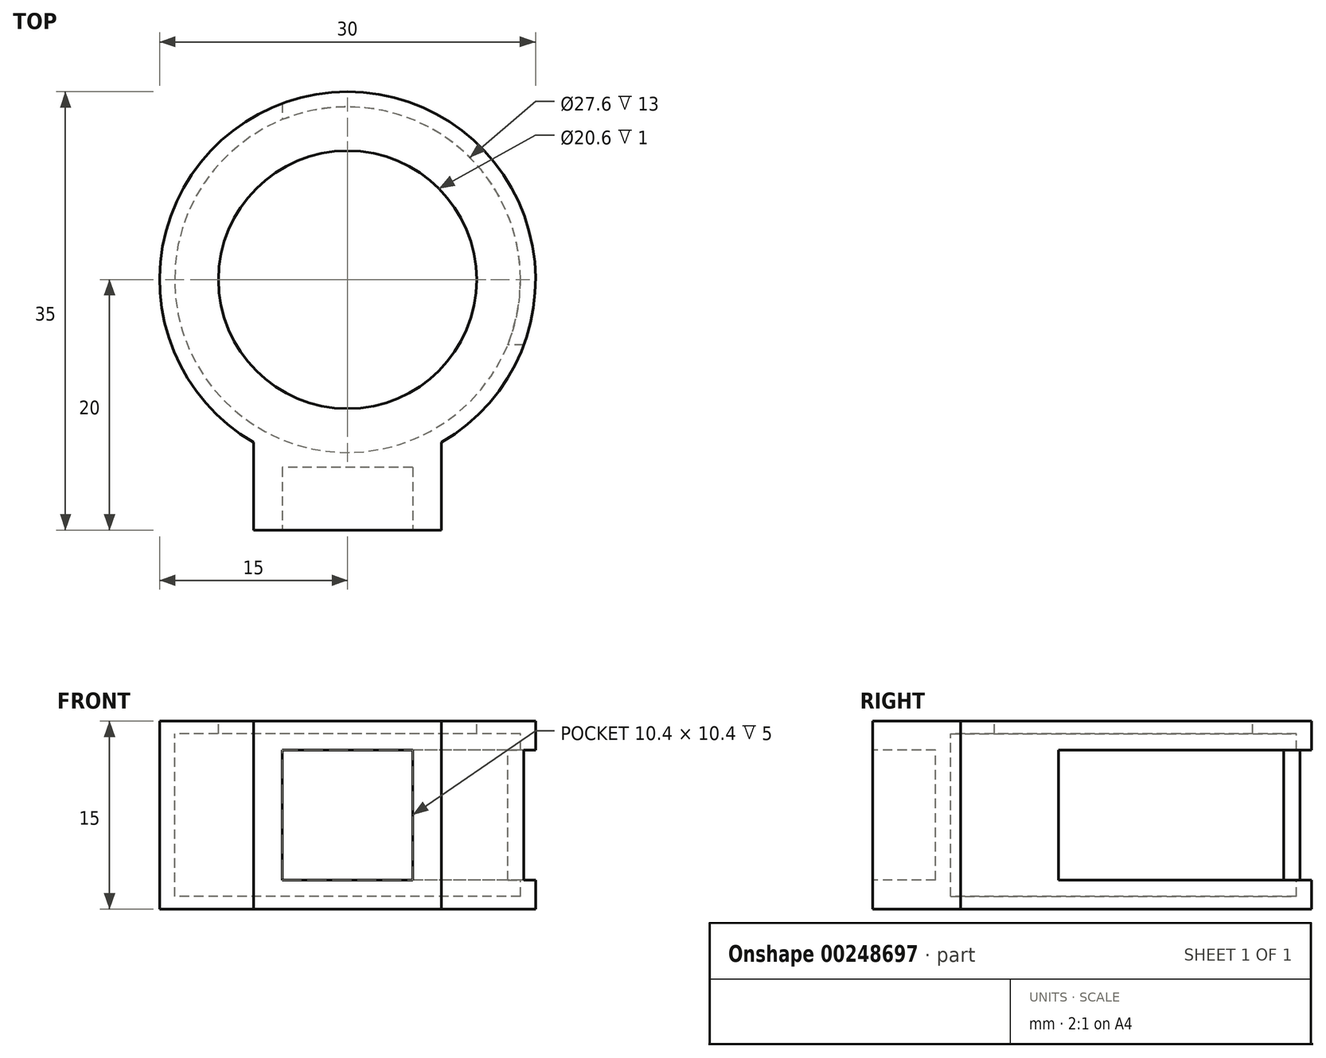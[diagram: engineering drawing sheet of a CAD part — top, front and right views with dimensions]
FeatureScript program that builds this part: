
annotation { "Feature Type Name" : "Feature", "Feature Type Description" : "" }
export const myFeature = defineFeature(function(context is Context, id is Id, definition is map)
    precondition{}
    {
        {
            var Q0;
            Q0=qCreatedBy(makeId("Top.planeOp"),FACE);
            var sketch = newSketch(context, id + "F0", { "sketchPlane" : qUnion([Q0])});
            skCircle(sketch, "E0", {"center": v(0, 0) * mm, "radius": 15 * mm});
            skSolve(sketch);
        }
        {
            var Q0;
            Q0 = qSketchRegion(id + "F0", true);
            extrude(context, id + "F1", {"entities" : qUnion([Q0]), "depth" : 15 * mm});
        }
        {
            var Q0;
            Q0=qCreatedBy(makeId("Front.planeOp"),FACE);
            var sketch = newSketch(context, id + "F2", { "sketchPlane" : qUnion([Q0])});
            skLineSegment(sketch, "E1.bottom", {"start": v(7.5, 0) * mm, "end": v(-7.5, 0) * mm});
            skLineSegment(sketch, "E1.top", {"start": v(7.5, 15) * mm, "end": v(-7.5, 15) * mm});
            skLineSegment(sketch, "E1.left", {"start": v(7.5, 0) * mm, "end": v(7.5, 15) * mm});
            skLineSegment(sketch, "E1.right", {"start": v(-7.5, 0) * mm, "end": v(-7.5, 15) * mm});
            skPoint(sketch, "E1.middle", {"position": v(0, 7.5) * mm});
            skSolve(sketch);
        }
        {
            var Q0;
            Q0 = qSketchRegion(id + "F2", true);
            extrude(context, id + "F3", {"entities" : qUnion([Q0]), "operationType" : NewBodyOperationType.ADD, "depth" : 20 * mm});
        }
        {
            var Q0;
            Q0=makeQuery(id+"F3.opExtrude","CAP_FACE",FACE,{"disambiguationData":[OSD([sQuery(id+"F2.wireOp",EDGE,"E1.bottom"),sQuery(id+"F2.wireOp",EDGE,"E1.top"),sQuery(id+"F2.wireOp",EDGE,"E1.left"),sQuery(id+"F2.wireOp",EDGE,"E1.right")])],"isStart":false});
            var sketch = newSketch(context, id + "F4", { "sketchPlane" : qUnion([Q0])});
            skLineSegment(sketch, "E2.bottom", {"start": v(5.2, 2.3) * mm, "end": v(-5.2, 2.3) * mm});
            skLineSegment(sketch, "E2.top", {"start": v(5.2, 12.7) * mm, "end": v(-5.2, 12.7) * mm});
            skLineSegment(sketch, "E2.left", {"start": v(5.2, 2.3) * mm, "end": v(5.2, 12.7) * mm});
            skLineSegment(sketch, "E2.right", {"start": v(-5.2, 2.3) * mm, "end": v(-5.2, 12.7) * mm});
            skPoint(sketch, "E2.middle", {"position": v(0, 7.5) * mm});
            skPoint(sketch, "E2.middle.positionSnap0", {"position": v(0, 15) * mm});
            skPoint(sketch, "E2.middle.positionSnap1", {"position": v(-7.5, 7.5) * mm});
            skPoint(sketch, "E2.centerSnap0", {"position": v(0, 15) * mm});
            skPoint(sketch, "E2.centerSnap1", {"position": v(-7.5, 7.5) * mm});
            skSolve(sketch);
        }
        {
            var Q0;
            Q0 = qSketchRegion(id + "F4", true);
            extrude(context, id + "F5", {"entities" : qUnion([Q0]), "operationType" : NewBodyOperationType.REMOVE, "oppositeDirection" : true, "depth" : 5 * mm});
        }
        {
            var Q0;
            Q0=makeQuery(id+"F3.boolean.opBoolean","MERGE",FACE,{"derivedFrom":[makeQuery(id+"F1.opExtrude","CAP_FACE",FACE,{"disambiguationData":[OSD([sQuery(id+"F0.wireOp",EDGE,"E0")])],"isStart":false}),makeQuery(id+"F3.opExtrude","SWEPT_FACE",FACE,{"disambiguationData":[OSD([sQuery(id+"F2.wireOp",EDGE,"E1.top")])]})]});
            var sketch = newSketch(context, id + "F6", { "sketchPlane" : qUnion([Q0])});
            skCircle(sketch, "E3", {"center": v(0, 0) * mm, "radius": 13.8 * mm});
            skSolve(sketch);
        }
        {
            var Q0;
            Q0 = qSketchRegion(id + "F6", true);
            extrude(context, id + "F7", {"entities" : qUnion([Q0]), "operationType" : NewBodyOperationType.REMOVE, "oppositeDirection" : true, "depth" : 14 * mm, "hasSecondDirection" : true, "secondDirectionOppositeDirection" : true, "secondDirectionDepth" : 1 * mm});
        }
        {
            var Q0;
            Q0=makeQuery(id+"F3.boolean.opBoolean","MERGE",FACE,{"derivedFrom":[makeQuery(id+"F1.opExtrude","CAP_FACE",FACE,{"disambiguationData":[OSD([sQuery(id+"F0.wireOp",EDGE,"E0")])],"isStart":false}),makeQuery(id+"F3.opExtrude","SWEPT_FACE",FACE,{"disambiguationData":[OSD([sQuery(id+"F2.wireOp",EDGE,"E1.top")])]})]});
            var sketch = newSketch(context, id + "F8", { "sketchPlane" : qUnion([Q0])});
            skCircle(sketch, "E4", {"center": v(0, 0) * mm, "radius": 10.3 * mm});
            skSolve(sketch);
        }
        {
            var Q0;
            Q0 = qSketchRegion(id + "F8", true);
            extrude(context, id + "F9", {"entities" : qUnion([Q0]), "operationType" : NewBodyOperationType.REMOVE, "oppositeDirection" : true, "depth" : 2 * mm});
        }
        {
            var Q0;
            Q0=makeQuery(id+"F3.boolean.opBoolean","MERGE",FACE,{"derivedFrom":[makeQuery(id+"F1.opExtrude","CAP_FACE",FACE,{"disambiguationData":[OSD([sQuery(id+"F0.wireOp",EDGE,"E0")])],"isStart":false}),makeQuery(id+"F3.opExtrude","SWEPT_FACE",FACE,{"disambiguationData":[OSD([sQuery(id+"F2.wireOp",EDGE,"E1.top")])]})]});
            var sketch = newSketch(context, id + "F10", { "sketchPlane" : qUnion([Q0])});
            skArc(sketch, "E5.0", {"start": v(7.5, -13) * mm, "mid": v(0, 15) * mm, "end": v(-7.5, -13) * mm});
            skLineSegment(sketch, "E6.bottom", {"start": v(5.2, 19.13) * mm, "end": v(-5.2, 19.13) * mm});
            skLineSegment(sketch, "E6.top", {"start": v(5.2, 1.47) * mm, "end": v(-5.2, 1.47) * mm});
            skLineSegment(sketch, "E6.left", {"start": v(5.2, 19.13) * mm, "end": v(5.2, 1.47) * mm});
            skLineSegment(sketch, "E6.right", {"start": v(-5.2, 19.13) * mm, "end": v(-5.2, 1.47) * mm});
            skPoint(sketch, "E6.middle", {"position": v(0, 10.3) * mm});
            skLineSegment(sketch, "E7.bottom", {"start": v(18.03, -5.2) * mm, "end": v(0.16, -5.2) * mm});
            skLineSegment(sketch, "E7.top", {"start": v(18.03, 5.2) * mm, "end": v(0.16, 5.2) * mm});
            skLineSegment(sketch, "E7.left", {"start": v(18.03, -5.2) * mm, "end": v(18.03, 5.2) * mm});
            skLineSegment(sketch, "E7.right", {"start": v(0.16, -5.2) * mm, "end": v(0.16, 5.2) * mm});
            skPoint(sketch, "E7.middle", {"position": v(9.1, 0) * mm});
            skSolve(sketch);
        }
        {
            var Q0;
            {var subQ0=sQuery(id+"F10.wireOp",EDGE,"E6.left");var subQ1=sQuery(id+"F10.wireOp",EDGE,"E5.0");var subQ2=makeQuery(id+"F10.imprint","INTERSECT",VERTEX,{"derivedFrom":[subQ1,subQ0]});Q0=makeQuery(id+"F10.imprint","IMPRINT",FACE,{"disambiguationData":[TD([[makeQuery(id+"F10.imprint","IMPRINT",EDGE,{"disambiguationData":[TD([[subQ2,-1.0]])],"derivedFrom":subQ1}),1.0]])]});}
            var Q1;
            {var subQ0=sQuery(id+"F10.wireOp",EDGE,"E7.top");var subQ1=sQuery(id+"F10.wireOp",EDGE,"E5.0");var subQ2=makeQuery(id+"F10.imprint","INTERSECT",VERTEX,{"derivedFrom":[subQ1,subQ0]});Q1=makeQuery(id+"F10.imprint","IMPRINT",FACE,{"disambiguationData":[TD([[makeQuery(id+"F10.imprint","IMPRINT",EDGE,{"disambiguationData":[TD([[subQ2,-1.0]])],"derivedFrom":subQ1}),1.0]])]});}
            var Q2;
            {var subQ0=sQuery(id+"F10.wireOp",EDGE,"E7.top");var subQ1=sQuery(id+"F10.wireOp",EDGE,"E5.0");var subQ2=makeQuery(id+"F10.imprint","INTERSECT",VERTEX,{"derivedFrom":[subQ1,subQ0]});Q2=makeQuery(id+"F10.imprint","IMPRINT",FACE,{"disambiguationData":[TD([[makeQuery(id+"F10.imprint","IMPRINT",EDGE,{"disambiguationData":[TD([[subQ2,1.0]])],"derivedFrom":subQ1}),1.0]])]});}
            extrude(context, id + "F11", {"entities" : qUnion([Q0, Q1, Q2]), "operationType" : NewBodyOperationType.REMOVE, "oppositeDirection" : true, "depth" : (15 - 2.3) * mm, "hasSecondDirection" : true, "secondDirectionOppositeDirection" : true, "secondDirectionDepth" : 2.3 * mm});
        }
    });
